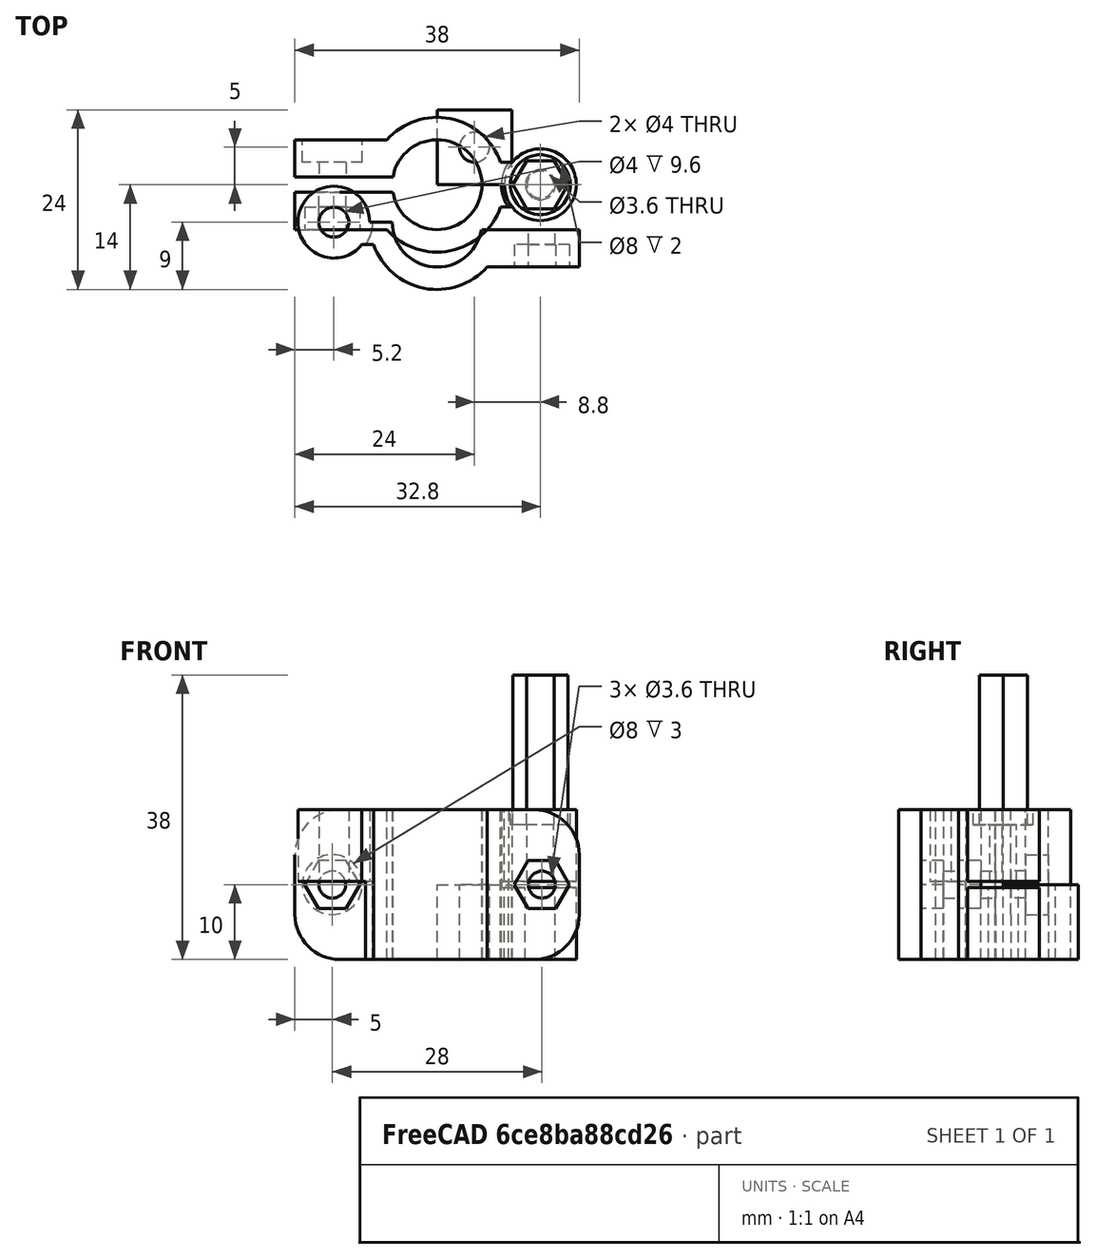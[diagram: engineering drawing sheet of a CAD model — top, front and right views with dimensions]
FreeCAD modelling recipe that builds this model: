
FCSTD DOCUMENT  (FreeCAD 0.18.4R)
Label: pipe_attach_v3
License: All rights reserved
LicenseURL: http://en.wikipedia.org/wiki/All_rights_reserved
objects: Part::Cylinder×10, Part::MultiFuse×4, Part::Cut×4, PartDesign::FeatureBase×4, PartDesign::Body×4, Part::Box×3, Part::Mirroring×2, Spreadsheet::Sheet×1, Part::Fillet×1, Part::RegularPolygon×1, Part::Extrusion×1, Part::Compound×1, Part::Feature×1
note: 36 computed .brp shape members not serialized (recipe doc carries the construction recipe); baked Part::Feature solids carry a one-line shape summary decoded from their .brp

FEATURE [Spreadsheet::Sheet] Spreadsheet  label="p001"
  cells = A1=internal_r; B1(internal_r)=6; A2=wall; B2(wall)=3; A3=length; B3(length)=20; A4=hole_r; B4(hole_r)=1.8; A5=petal_size; B5(petal_size)=10; A6=bolt_head_nut_height; B6(bolt_head_nut_height)=2; A7=bolt_head_r; B7(bolt_head_r)=4; A8=m3_nut_circumradius; B8(m3_nut_circumradius)=3.7; A9=bolt_insert_r; B9(bolt_insert_r)=2; A10=petal_offset; B10(petal_offset)=1; A11=external_cylinder_angle_offset; B11(external_cylinder_angle_offset)=10
FEATURE [Part::Cylinder] Cylinder  label="external cylinder"
  Angle = 170
  AttacherType = Attacher::AttachEngine3D
  Height = 20
  Radius = 9
  expr: Radius = p001.internal_r + p001.wall
  expr: Angle = 180 - p001.external_cylinder_angle_offset
  expr: Height = p001.length
FEATURE [Part::Cylinder] Cylinder001  label="hole cylinder"
  Angle = 180
  AttacherType = Attacher::AttachEngine3D
  Height = 20
  Radius = 6
  expr: Radius = p001.internal_r
  expr: Height = p001.length
FEATURE [Part::Cylinder] Cylinder002  label="side cylinder"
  Angle = 360
  AttacherType = Attacher::AttachEngine3D
  Height = 20
  Placement = pos=(13.8,0,0) rot=(0,0,1;0rad)
  Radius = 4.8
  expr: Placement.Base.x = p001.internal_r + p001.wall + p001.wall + p001.hole_r
  expr: Height = p001.length
  expr: Radius = p001.hole_r + p001.wall
FEATURE [Part::Box] Box  label="petal cube"
  AttacherType = Attacher::AttachEngine3D
  Height = 20
  Length = 13
  Placement = pos=(-19,1,0) rot=(0,0,1;0rad)
  Width = 5
  expr: Width = p001.wall + p001.bolt_head_nut_height
  expr: Placement.Base.y = p001.petal_offset
  expr: Placement.Base.x = -(p001.internal_r + p001.wall + p001.petal_size)
  expr: Height = p001.length
  expr: Length = p001.petal_size + p001.wall
FEATURE [Part::Fillet] Fillet  label="petal fillet"
  Base = -> Box
  Edges = 2 edges r=6: [Edge2,Edge4]
FEATURE [Part::Box] Box001  label="side cube"
  AttacherType = Attacher::AttachEngine3D
  Height = 20
  Length = 7.8
  Placement = pos=(6,0,0) rot=(0,0,1;0rad)
  Width = 3
  expr: Placement.Base.x = p001.internal_r
  expr: Width = p001.wall
  expr: Height = p001.length
  expr: Length = p001.hole_r + p001.wall * 2
FEATURE [Part::Cylinder] Cylinder003  label="bolt hole"
  Angle = 360
  AttacherType = Attacher::AttachEngine3D
  Height = 50
  Placement = pos=(-14,20,10) rot=(1,0,0;1.5708rad)
  Radius = 1.8
  expr: Placement.Base.z = p001.length / 2
  expr: Placement.Base.x = -(p001.internal_r + p001.wall + p001.petal_size / 2)
  expr: Radius = p001.hole_r
FEATURE [Part::Cylinder] Cylinder004  label="horizontal bolt hole"
  Angle = 360
  AttacherType = Attacher::AttachEngine3D
  Height = 20
  Placement = pos=(13.8,0,0) rot=(0,0,1;0rad)
  Radius = 1.8
  expr: Height = p001.length
  expr: Placement.Base.x = p001.internal_r + p001.wall * 2 + p001.hole_r
  expr: Radius = p001.hole_r
FEATURE [Part::MultiFuse] Fusion  label="hole fusion"
  Shapes = -> [Cylinder004,Cylinder003,Cylinder001]
FEATURE [Part::MultiFuse] Fusion001  label="half fusion"
  Shapes = -> [Box001,Fillet,Cylinder002,Cylinder]
FEATURE [Part::Cut] Cut  label="attach half"
  Base = -> Fusion001
  Tool = -> Fusion
FEATURE [Part::Mirroring] Part__Mirroring  label="attach half (Mirror #1)"
  Base = (0,0,0)
  Normal = (0,1,0)
  Source = -> Cut
FEATURE [Part::Cylinder] Cylinder005  label="side half cut cylinder"
  Angle = 360
  AttacherType = Attacher::AttachEngine3D
  Height = 10.4
  Placement = pos=(13.8,0,0) rot=(0,0,1;0rad)
  Radius = 5.2
  expr: Placement.Base.x = p001.internal_r + p001.wall + p001.wall + p001.hole_r
  expr: Height = p001.length / 2 + 0.4
  expr: Radius = p001.wall + p001.hole_r + 0.4
FEATURE [Part::Mirroring] Part__Mirroring001  label="side half cut cylinder (Mirror #2)"
  Base = (0,0,10)
  Normal = (0,0,1)
  Source = -> Cylinder005
  expr: Base.z = p001.length / 2
FEATURE [Part::Cylinder] Cylinder095  label="bolt head cylinder"
  Angle = 360
  AttacherType = Attacher::AttachEngine3D
  Height = 20
  Placement = pos=(-14,3,10) rot=(-1,0,0;1.5708rad)
  Radius = 4
  expr: Placement.Base.z = p001.length / 2
  expr: Placement.Base.y = p001.wall
  expr: Placement.Base.x = -(p001.internal_r + p001.wall + p001.petal_size / 2)
  expr: Radius = p001.bolt_head_r
FEATURE [Part::RegularPolygon] RegularPolygon003  label="m3 nut polygon"
  AttacherType = Attacher::AttachEngine3D
  Circumradius = 3.7
  Polygon = 6
  expr: Circumradius = p001.m3_nut_circumradius
FEATURE [Part::Extrusion] Extrude003  label="m3 nut hole"
  Base = -> RegularPolygon003
  Dir = (0,0,1)
  DirMode = 2
  FaceMakerClass = Part::FaceMakerBullseye
  LengthFwd = 20
  LengthRev = 0
  Solid = true
  Symmetric = false
FEATURE [PartDesign::FeatureBase] Clone
  BaseFeature = -> Extrude003
FEATURE [PartDesign::Body] Body  label="m3 nut hole side clone"
  BaseFeature = -> Extrude003
  Group = -> [Clone]
  Origin = -> Origin001
  Placement = pos=(13.8,0,18) rot=(0,0,1;0rad)
  Tip = -> Clone
  expr: Placement.Base.z = p001.length - p001.bolt_head_nut_height
  expr: Placement.Base.x = p001.internal_r + p001.wall * 2 + p001.hole_r
FEATURE [PartDesign::FeatureBase] Clone001
  BaseFeature = -> Extrude003
FEATURE [PartDesign::Body] Body001  label="m3 nut hole petal clone"
  BaseFeature = -> Extrude003
  Group = -> [Clone001]
  Origin = -> Origin002
  Placement = pos=(-14,-3,10) rot=(1,0,0;1.5708rad)
  Tip = -> Clone001
  expr: Placement.Base.z = p001.length / 2
  expr: Placement.Base.y = -p001.wall
  expr: Placement.Base.x = -(p001.internal_r + p001.wall + p001.petal_size / 2)
FEATURE [Part::Cylinder] Cylinder096  label="bolt head side cylinder"
  Angle = 360
  AttacherType = Attacher::AttachEngine3D
  Height = 2
  Placement = pos=(13.8,0,18) rot=(0,0,1;0rad)
  Radius = 4
  expr: Placement.Base.z = p001.length - p001.bolt_head_nut_height
  expr: Height = p001.bolt_head_nut_height
  expr: Placement.Base.x = p001.internal_r + p001.wall * 2 + p001.hole_r
  expr: Radius = p001.bolt_head_r
FEATURE [Part::MultiFuse] Fusion002  label="top half remove fusion"
  Shapes = -> [Cylinder005,Cylinder095,Cylinder096]
FEATURE [Part::Cut] Cut001  label="top half cut"
  Base = -> Cut
  Tool = -> Fusion002
FEATURE [PartDesign::FeatureBase] Clone002
  BaseFeature = -> Cut001
FEATURE [PartDesign::Body] Body002  label="top half clone"
  BaseFeature = -> Cut001
  Group = -> [Clone002]
  Origin = -> Origin003
  Tip = -> Clone002
FEATURE [Part::Box] Box002  label="Cube"
  AttacherType = Attacher::AttachEngine3D
  Height = 10
  Length = 10
  Width = 10
FEATURE [Part::Cylinder] Cylinder097  label="Cylinder"
  Angle = 360
  AttacherType = Attacher::AttachEngine3D
  Height = 10
  Placement = pos=(5,5,0) rot=(0,0,1;0rad)
  Radius = 2
FEATURE [Part::Cut] Cut003  label="test_hole"
  Base = -> Box002
  Tool = -> Cylinder097
FEATURE [Part::Cylinder] Cylinder098  label="bolt insert hole"
  Angle = 360
  AttacherType = Attacher::AttachEngine3D
  Height = 10
  Placement = pos=(13.8,0,0) rot=(0,0,1;0rad)
  Radius = 2
  expr: Height = p001.length / 2
  expr: Placement.Base.x = p001.internal_r + p001.wall * 2 + p001.hole_r
  expr: Radius = p001.bolt_insert_r
FEATURE [Part::MultiFuse] Fusion003  label="botom half remove fusion"
  Shapes = -> [Part__Mirroring001,Body001,Cylinder098]
FEATURE [Part::Cut] Cut002  label="bottom half cut"
  Base = -> Part__Mirroring
  Tool = -> Fusion003
FEATURE [PartDesign::FeatureBase] Clone003
  BaseFeature = -> Cut002
FEATURE [PartDesign::Body] Body003  label="bottom half clone"
  BaseFeature = -> Cut002
  Group = -> [Clone003]
  Origin = -> Origin004
  Placement = pos=(0,-5,20) rot=(0,1,0;3.14159rad)
  Tip = -> Clone003
  expr: Placement.Base.z = p001.length
FEATURE [Part::Compound] Compound  label="halves compound"
  Links = -> [Body003,Body002]
FEATURE [Part::Feature] Cut002001  label="bottom half cut shape"
  shape: bbox 37.6 x 13.8 x 20 mm, 25 faces (baked)
